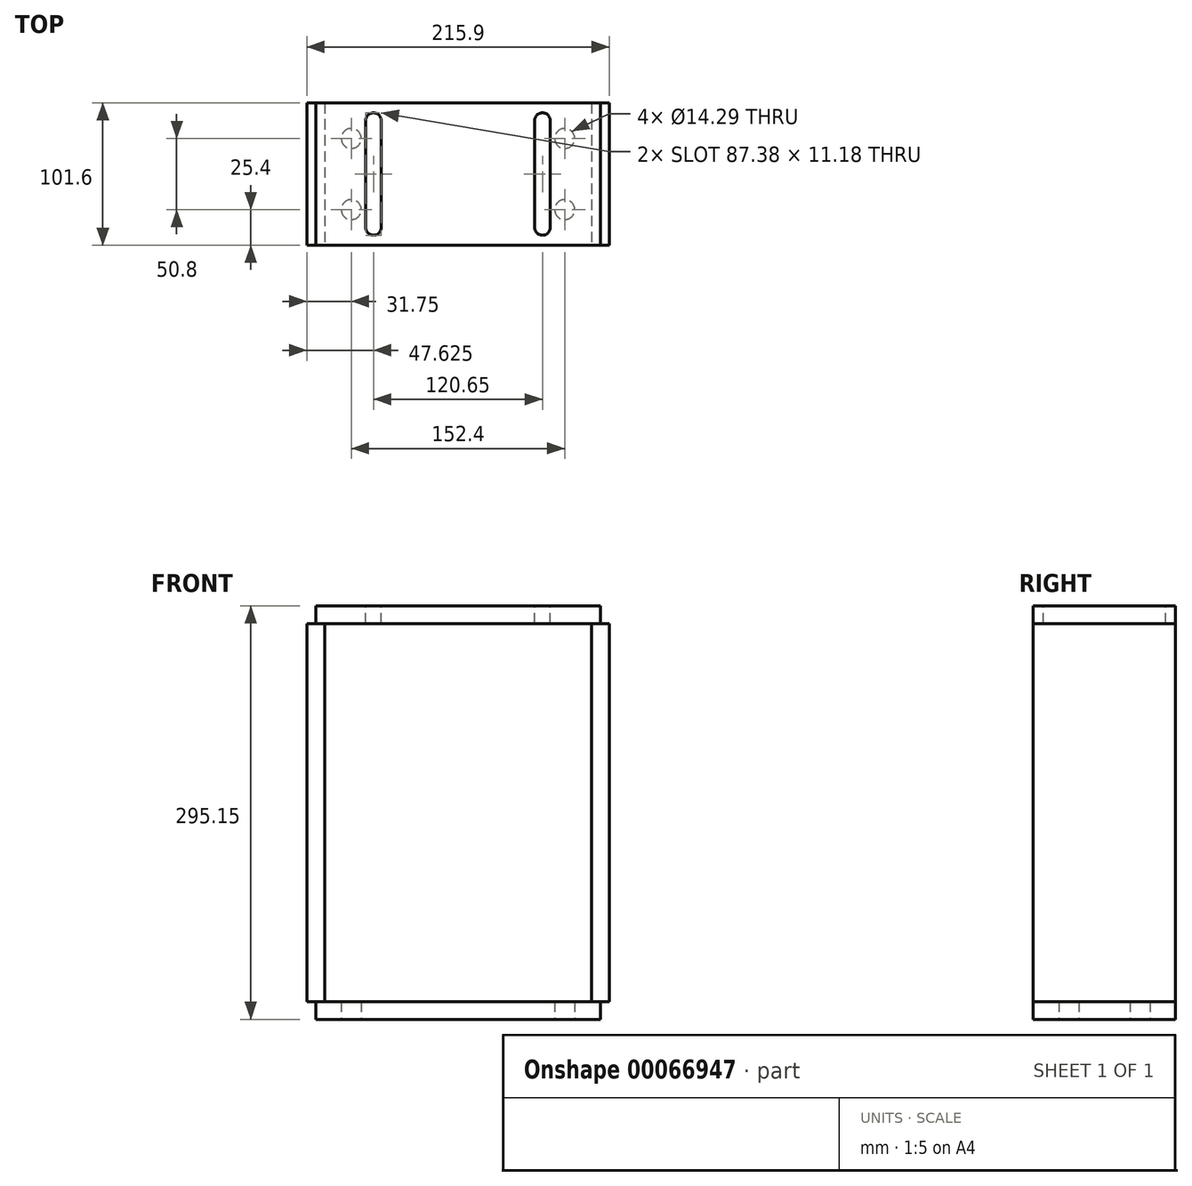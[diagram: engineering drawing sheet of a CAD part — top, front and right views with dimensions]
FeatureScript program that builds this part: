
annotation { "Feature Type Name" : "Feature", "Feature Type Description" : "" }
export const myFeature = defineFeature(function(context is Context, id is Id, definition is map)
    precondition{}
    {
        {
            var Q0;
            Q0=qCreatedBy(makeId("Top.planeOp"),FACE);
            var sketch = newSketch(context, id + "F0", { "sketchPlane" : qUnion([Q0])});
            skLineSegment(sketch, "E0.rect.bottom", {"start": v(-101.6, 50.8) * mm, "end": v(101.6, 50.8) * mm});
            skLineSegment(sketch, "E0.rect.top", {"start": v(-101.6, -50.8) * mm, "end": v(101.6, -50.8) * mm});
            skLineSegment(sketch, "E0.rect.left", {"start": v(-101.6, 50.8) * mm, "end": v(-101.6, -50.8) * mm});
            skLineSegment(sketch, "E0.rect.right", {"start": v(101.6, 50.8) * mm, "end": v(101.6, -50.8) * mm});
            skPoint(sketch, "E0.rect.middle", {"position": v(0, 0) * mm});
            skLineSegment(sketch, "E1", {"start": v(0, 50.8) * mm, "end": v(0, -50.8) * mm, "construction": true});
            skLineSegment(sketch, "E2", {"start": v(-101.6, 0) * mm, "end": v(101.6, 0) * mm, "construction": true});
            skLineSegment(sketch, "E3.0", {"start": v(-76.2, 50.8) * mm, "end": v(-76.2, -50.8) * mm, "construction": true});
            skLineSegment(sketch, "E4.0", {"start": v(-101.6, -25.4) * mm, "end": v(101.6, -25.4) * mm, "construction": true});
            skPoint(sketch, "E5", {"position": v(-76.2, -25.4) * mm});
            skPoint(sketch, "E6.0.1.0", {"position": v(-76.2, 25.4) * mm});
            skPoint(sketch, "E6.1.0.0", {"position": v(76.2, -25.4) * mm});
            skPoint(sketch, "E6.1.1.0", {"position": v(76.2, 25.4) * mm});
            skLineSegment(sketch, "E6.direction1", {"start": v(-76.2, -25.4) * mm, "end": v(76.2, -25.4) * mm, "construction": true});
            skLineSegment(sketch, "E6.direction2", {"start": v(-76.2, -25.4) * mm, "end": v(-76.2, 25.4) * mm, "construction": true});
            skSolve(sketch);
        }
        {
            var Q0;
            Q0=makeQuery(id+"F0.imprint","IMPRINT",FACE,{"disambiguationData":[TD([[makeQuery(id+"F0.imprint","IMPRINT",EDGE,{"derivedFrom":sQuery(id+"F0.wireOp",EDGE,"E0.rect.bottom")}),-1.0]])]});
            extrude(context, id + "F1", {"entities" : qUnion([Q0]), "depth" : 12.7 * mm});
        }
        {
            var Q0;
            Q0=sQuery(id+"F0.wireOp",VERTEX,"E5");
            var Q1;
            Q1=sQuery(id+"F0.wireOp",VERTEX,"E6.0.1.0");
            var Q2;
            Q2=sQuery(id+"F0.wireOp",VERTEX,"E6.1.1.0");
            var Q3;
            Q3=sQuery(id+"F0.wireOp",VERTEX,"E6.1.0.0");
            var Q4;
            Q4=makeQuery(id+"F1.opExtrude","SWEPT_BODY",BODY,{"disambiguationData":[OSD([sQuery(id+"F0.wireOp",EDGE,"E0.rect.bottom"),sQuery(id+"F0.wireOp",EDGE,"E0.rect.top"),sQuery(id+"F0.wireOp",EDGE,"E0.rect.left"),sQuery(id+"F0.wireOp",EDGE,"E0.rect.right")])]});
            hole(context, id + "F2", {"style" : HoleStyle.SIMPLE, "holeDiameter" : 14.29 * mm, "endStyle" : HoleEndStyle.THROUGH, "oppositeDirection" : true, "locations" : qUnion([Q0, Q1, Q2, Q3]), "scope" : qUnion([Q4])});
        }
        {
            var Q0;
            Q0=qCreatedBy(makeId("Top.planeOp"),FACE);
            cPlane(context, id + "F3", {"entities" : qUnion([Q0]), "cplaneType" : CPlaneType.OFFSET, "offset" : 295.15 * mm, "width" : 152.4 * mm, "height" : 152.4 * mm});
        }
        {
            var Q0;
            Q0=qCreatedBy(id+"F3.planeOp",FACE);
            var sketch = newSketch(context, id + "F4", { "sketchPlane" : qUnion([Q0])});
            skLineSegment(sketch, "E7.0", {"start": v(-101.6, 50.8) * mm, "end": v(101.6, 50.8) * mm});
            skLineSegment(sketch, "E8.0", {"start": v(-101.6, 50.8) * mm, "end": v(-101.6, -50.8) * mm});
            skLineSegment(sketch, "E9.0", {"start": v(-101.6, -50.8) * mm, "end": v(101.6, -50.8) * mm});
            skLineSegment(sketch, "E10.0", {"start": v(101.6, 50.8) * mm, "end": v(101.6, -50.8) * mm});
            skLineSegment(sketch, "E11", {"start": v(-101.6, 0) * mm, "end": v(101.6, 0) * mm, "construction": true});
            skLineSegment(sketch, "E12", {"start": v(0, 50.8) * mm, "end": v(0, -50.8) * mm, "construction": true});
            skLineSegment(sketch, "E13.0", {"start": v(-60.32, 38.1) * mm, "end": v(-60.33, -38.1) * mm, "construction": true});
            skLineSegment(sketch, "E14.0", {"start": v(-101.6, 38.1) * mm, "end": v(101.6, 38.1) * mm, "construction": true});
            skLineSegment(sketch, "E15.0", {"start": v(-101.6, -38.1) * mm, "end": v(101.6, -38.1) * mm, "construction": true});
            skArc(sketch, "E16.0.startCap", {"start": v(-65.91, 38.1) * mm, "mid": v(-60.32, 43.69) * mm, "end": v(-54.74, 38.1) * mm});
            skArc(sketch, "E16.0.endCap", {"start": v(-54.74, -38.1) * mm, "mid": v(-60.33, -43.69) * mm, "end": v(-65.91, -38.1) * mm});
            skLineSegment(sketch, "E16.0.left", {"start": v(-54.74, 38.1) * mm, "end": v(-54.74, -38.1) * mm});
            skLineSegment(sketch, "E16.0.right", {"start": v(-65.91, 38.1) * mm, "end": v(-65.91, -38.1) * mm});
            skArc(sketch, "E17.MirrorCS", {"start": v(65.91, 38.1) * mm, "mid": v(60.33, 43.69) * mm, "end": v(54.74, 38.1) * mm});
            skArc(sketch, "E18.MirrorCS", {"start": v(54.74, -38.1) * mm, "mid": v(60.32, -43.69) * mm, "end": v(65.91, -38.1) * mm});
            skLineSegment(sketch, "E19.MirrorCS", {"start": v(65.91, 38.1) * mm, "end": v(65.91, -38.1) * mm});
            skLineSegment(sketch, "E20.MirrorCS", {"start": v(54.74, 38.1) * mm, "end": v(54.74, -38.1) * mm});
            skLineSegment(sketch, "E21.MirrorCS", {"start": v(60.33, 38.1) * mm, "end": v(60.32, -38.1) * mm, "construction": true});
            skSolve(sketch);
        }
        {
            var Q0;
            Q0 = qSketchRegion(id + "F4", true);
            extrude(context, id + "F5", {"entities" : qUnion([Q0]), "oppositeDirection" : true, "depth" : 12.7 * mm});
        }
        {
            var Q0;
            Q0=makeQuery(id+"F5.opExtrude","SWEPT_FACE",FACE,{"disambiguationData":[OSD([sQuery(id+"F4.wireOp",EDGE,"E10.0")])]});
            var sketch = newSketch(context, id + "F6", { "sketchPlane" : qUnion([Q0])});
            skLineSegment(sketch, "E22.0", {"start": v(50.8, 282.45) * mm, "end": v(-50.8, 282.45) * mm, "construction": true});
            skLineSegment(sketch, "E23.0", {"start": v(50.8, 12.7) * mm, "end": v(-50.8, 12.7) * mm, "construction": true});
            skLineSegment(sketch, "E24.bottom", {"start": v(-50.8, 282.45) * mm, "end": v(50.8, 282.45) * mm});
            skLineSegment(sketch, "E24.top", {"start": v(-50.8, 12.7) * mm, "end": v(50.8, 12.7) * mm});
            skLineSegment(sketch, "E24.left", {"start": v(-50.8, 282.45) * mm, "end": v(-50.8, 12.7) * mm});
            skLineSegment(sketch, "E24.right", {"start": v(50.8, 282.45) * mm, "end": v(50.8, 12.7) * mm});
            skSolve(sketch);
        }
        {
            var Q0;
            Q0 = qSketchRegion(id + "F6", true);
            extrude(context, id + "F7", {"entities" : qUnion([Q0]), "endBound" : BoundingType.SYMMETRIC, "depth" : 12.7 * mm});
        }
        {
            var Q0;
            Q0=makeQuery(id+"F7.opExtrude","SWEPT_BODY",BODY,{"disambiguationData":[OSD([sQuery(id+"F6.wireOp",EDGE,"E24.bottom"),sQuery(id+"F6.wireOp",EDGE,"E24.top"),sQuery(id+"F6.wireOp",EDGE,"E24.left"),sQuery(id+"F6.wireOp",EDGE,"E24.right")])]});
            var Q1;
            Q1=qCreatedBy(makeId("Right.planeOp"),FACE);
            mirror(context, id + "F8", {"entities" : qUnion([Q0]), "mirrorPlane" : qUnion([Q1])});
        }
    });
